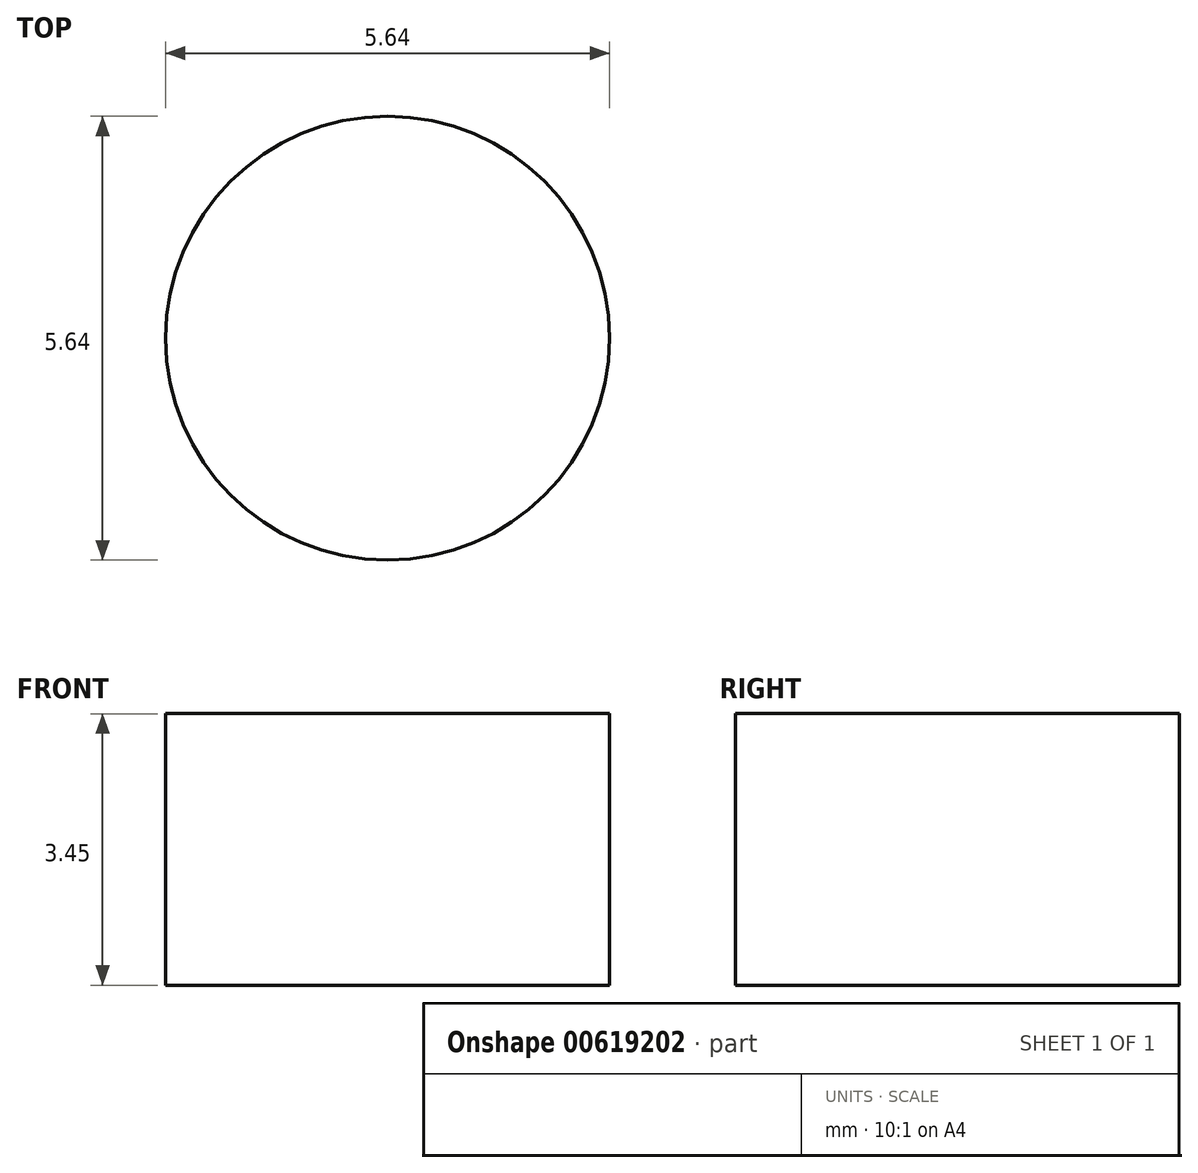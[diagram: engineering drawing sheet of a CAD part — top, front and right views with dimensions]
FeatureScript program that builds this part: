
annotation { "Feature Type Name" : "Feature", "Feature Type Description" : "" }
export const myFeature = defineFeature(function(context is Context, id is Id, definition is map)
    precondition{}
    {
        {
            var Q0;
            Q0=qCreatedBy(makeId("Top.planeOp"),FACE);
            var sketch = newSketch(context, id + "F0", { "sketchPlane" : qUnion([Q0])});
            skCircle(sketch, "E0", {"center": v(0, 0) * mm, "radius": 2.82 * mm});
            skSolve(sketch);
        }
        {
            var Q0;
            Q0=qSketchRegion(id+"F0",true);
            extrude(context, id + "F1", {"entities" : qUnion([Q0]), "depth" : 3.45 * mm});
        }
    });
